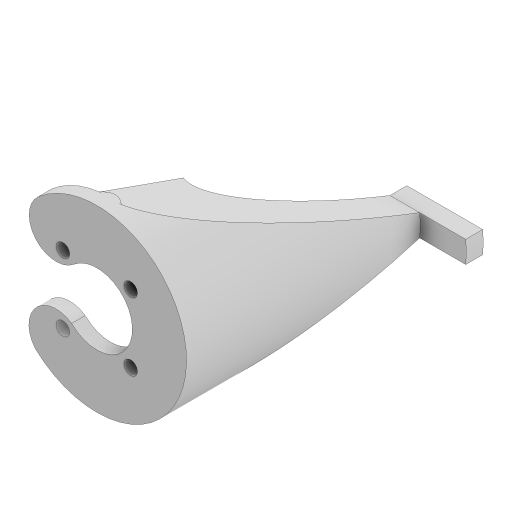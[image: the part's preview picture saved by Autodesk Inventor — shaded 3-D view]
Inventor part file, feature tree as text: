
AUTODESK INVENTOR PART (.ipt)
format: ipt  version: 2024 (Build 280153000, 153)  size: 436,736 bytes
history: native  units: mm
features: projected_geometry x14, extrude x10, sketch x9
ambient origin geometry x8: Origin, YZ Plane, XZ Plane, XY Plane, X Axis, Y Axis, Z Axis, Center Point
bodies: Solid1 (feature_tree)
feature tree (33):
  extrude  "Extrusion1"  Depth=2.0mm TaperAngle=0.0deg
  extrude  "Extrusion2"  Depth=10.0mm TaperAngle=0.0deg
  extrude  "Extrusion3"  Depth=40.0mm
  extrude  "Extrusion4"  Depth=5.0mm TaperAngle=0.0deg
  extrude  "Extrusion5"  Depth=10.5mm
  extrude  "Extrusion6"  Depth=36.9655mm
  extrude  "Extrusion7"  TaperAngle=0.0deg  [1 undecoded]
  extrude  "Extrusion8"  Depth=10.0mm TaperAngle=0.0deg
  extrude  "Extrusion9"  [1 undecoded]
  extrude  "Extrusion10"  [1 undecoded]
  sketch  "Sketch1"  dims[d0=21.0mm d1=2.0mm d2=0.0mm]
  sketch  "Sketch2"  dims[d3=10.0mm d4=0.0mm d5=62.0mm d6=0.0mm]
  projected_geometry  "Projected Loop1"
  projected_geometry  "Projected Loop7"
  projected_geometry  "Projected Loop8"
  projected_geometry  "Projected Loop9"
  projected_geometry  "Projected Loop10"
  projected_geometry  "Projected Loop11"
  sketch  "Sketch5"  dims[d7=40.0mm d8=1.22173mm]
  sketch  "Sketch6"  dims[d9=5.0mm d10=0.0mm d11=25.0mm d12=0.0mm]
  projected_geometry  "Projected Loop12"
  projected_geometry  "Projected Loop13"
  sketch  "Sketch7"  dims[d13=10.651mm d14=10.5mm]
  projected_geometry  "Projected Loop14"
  sketch  "Sketch8"  dims[d15=52.930509mm d16=36.9655mm]
  projected_geometry  "Projected Loop15"
  projected_geometry  "Projected Loop16"
  sketch  "Sketch9"  dims[d17=4.0mm d18=0.0mm d19=0.0mm d20=0.0mm]
  projected_geometry  "Projected Loop17"
  sketch  "Sketch10"  dims[d21=10.0mm d22=0.0mm d23=10.0mm d24=0.0mm]
  projected_geometry  "Projected Loop18"
  projected_geometry  "Projected Loop19"
  sketch  "Sketch11"  dims[d25=0.0mm d26=0.0mm]
note: 3 required parameter values undecoded (feature->parameter linkage not recoverable at this tier; creation-order binding heuristic only, values carry confidence <= 0.55)
